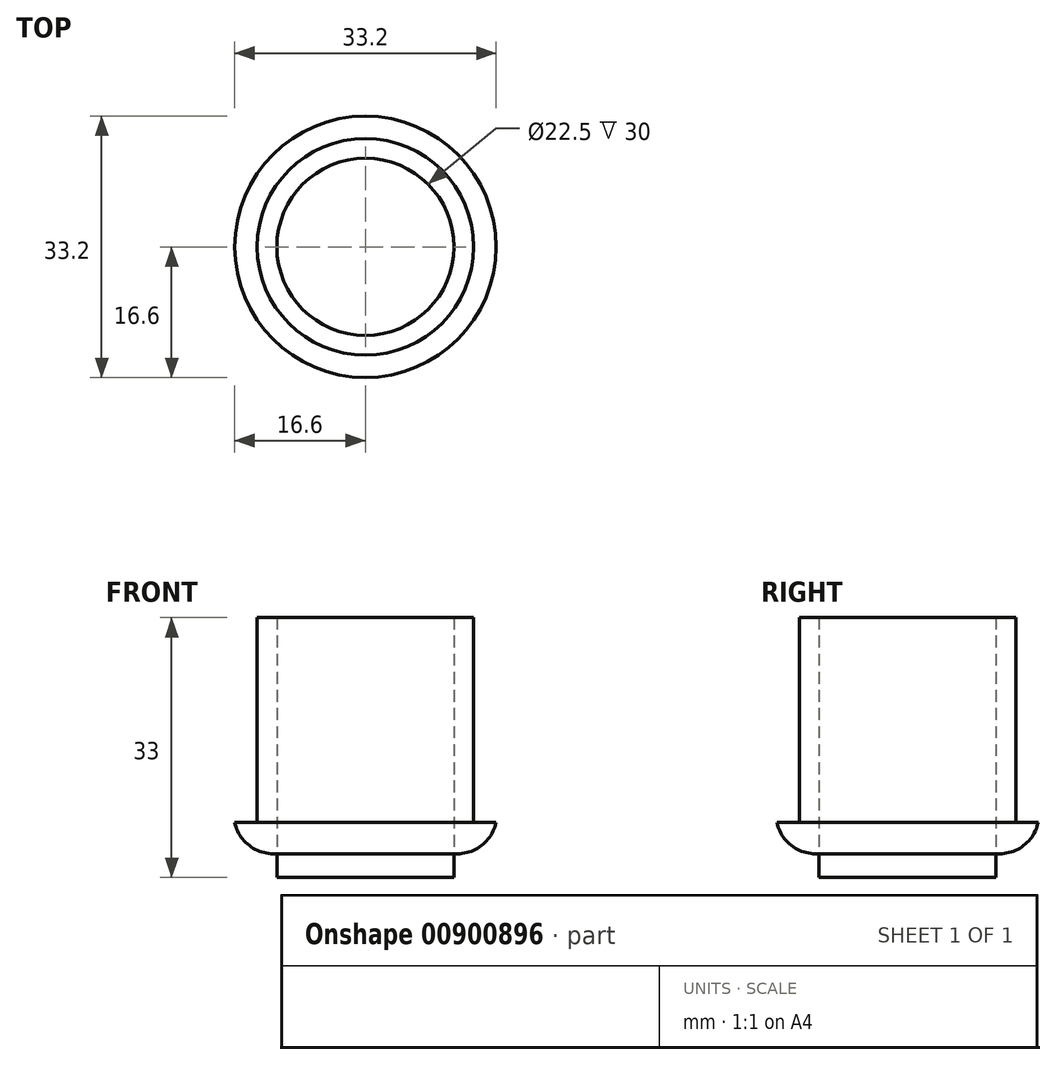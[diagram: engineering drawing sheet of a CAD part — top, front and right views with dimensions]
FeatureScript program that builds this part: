
annotation { "Feature Type Name" : "Feature", "Feature Type Description" : "" }
export const myFeature = defineFeature(function(context is Context, id is Id, definition is map)
    precondition{}
    {
        {
            var Q0;
            Q0=qCreatedBy(makeId("Top.planeOp"),FACE);
            var sketch = newSketch(context, id + "F0", { "sketchPlane" : qUnion([Q0])});
            skCircle(sketch, "E0", {"center": v(0, 0) * mm, "radius": 13.75 * mm});
            skCircle(sketch, "E1", {"center": v(0, 0) * mm, "radius": 16.6 * mm});
            skCircle(sketch, "E2", {"center": v(0, 0) * mm, "radius": 11.25 * mm});
            skSolve(sketch);
        }
        {
            var Q0;
            Q0=makeQuery(id+"F0.imprint","IMPRINT",FACE,{"disambiguationData":[TD([[makeQuery(id+"F0.imprint","IMPRINT",EDGE,{"derivedFrom":sQuery(id+"F0.wireOp",EDGE,"E0")}),1.0]])]});
            extrude(context, id + "F1", {"entities" : qUnion([Q0]), "depth" : 30 * mm, "offsetDistance" : 25 * mm});
        }
        {
            var Q0;
            Q0=makeQuery(id+"F0.imprint","IMPRINT",FACE,{"disambiguationData":[TD([[makeQuery(id+"F0.imprint","IMPRINT",EDGE,{"derivedFrom":sQuery(id+"F0.wireOp",EDGE,"E0")}),-1.0]])]});
            extrude(context, id + "F2", {"entities" : qUnion([Q0]), "operationType" : NewBodyOperationType.ADD, "depth" : 4 * mm, "offsetDistance" : 25 * mm});
        }
        {
            var Q0;
            Q0=makeQuery(id+"F2.opExtrude","CAP_EDGE",EDGE,{"disambiguationData":[OSD([sQuery(id+"F0.wireOp",EDGE,"E1")])],"isStart":true});
            fillet(context, id + "F3", {"entities" : qUnion([Q0]), "radius" : 5 * mm, "tangentPropagation" : true, "allowEdgeOverflow" : false});
        }
        {
            var Q0;
            Q0=makeQuery(id+"F0.imprint","IMPRINT",FACE,{"disambiguationData":[TD([[makeQuery(id+"F0.imprint","IMPRINT",EDGE,{"derivedFrom":sQuery(id+"F0.wireOp",EDGE,"E2")}),1.0]])]});
            extrude(context, id + "F4", {"entities" : qUnion([Q0]), "oppositeDirection" : true, "depth" : 3 * mm, "offsetDistance" : 25 * mm});
        }
    });
